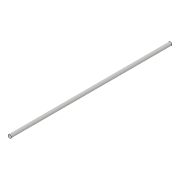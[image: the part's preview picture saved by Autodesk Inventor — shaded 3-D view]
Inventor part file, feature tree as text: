
AUTODESK INVENTOR PART (.ipt)
format: ipt  version: 2018.3 (Build 223284000, 284)  size: 69,120 bytes
history: native  units: in
note: dims shown in document units (in); Inventor stores cm internally (conversion verified against a paired STEP export)
features: extrude x1, sketch x1
ambient origin geometry x8: Origin, YZ Plane, XZ Plane, XY Plane, X Axis, Y Axis, Z Axis, Center Point
bodies: Solid1 (feature_tree)
feature tree (2):
  extrude  "Extrusion1"  Depth=6.0in TaperAngle=0.0deg
  sketch  "Sketch1"  dims[d0=0.125in d1=6.0in d2=0.0in]
